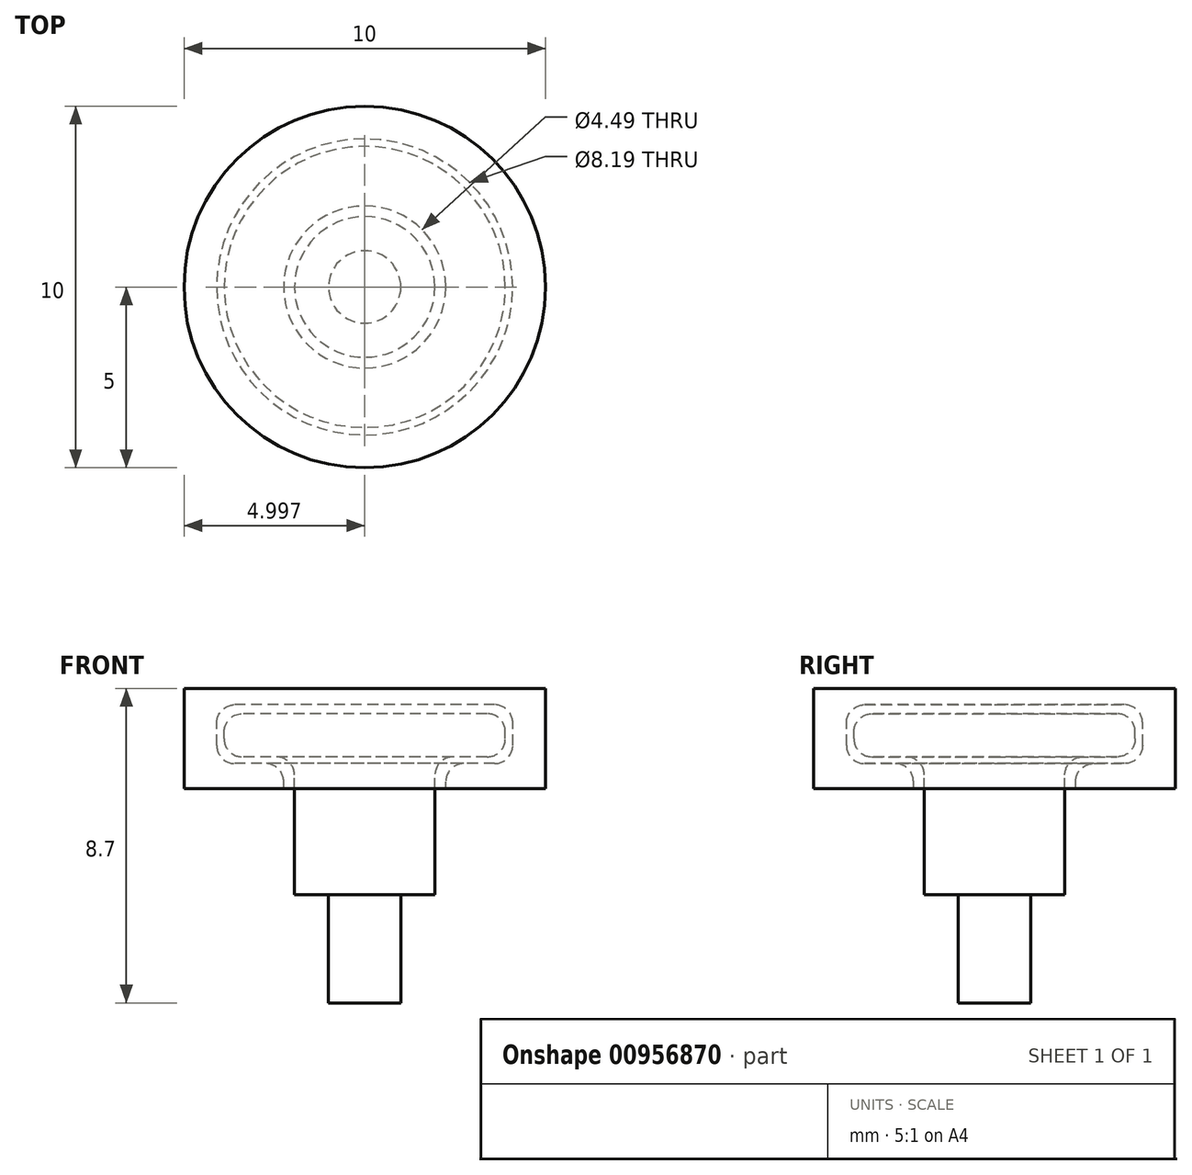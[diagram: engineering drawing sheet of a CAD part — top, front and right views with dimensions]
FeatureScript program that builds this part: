
annotation { "Feature Type Name" : "Feature", "Feature Type Description" : "" }
export const myFeature = defineFeature(function(context is Context, id is Id, definition is map)
    precondition{}
    {
        {
            var Q0;
            Q0=qCreatedBy(makeId("Front.planeOp"),FACE);
            var sketch = newSketch(context, id + "F0", { "sketchPlane" : qUnion([Q0])});
            skLineSegment(sketch, "E0.bottom", {"start": v(-2.43, 2.08) * mm, "end": v(0.96, 2.08) * mm});
            skLineSegment(sketch, "E0.top", {"start": v(-2.43, 0.88) * mm, "end": v(-1.49, 0.88) * mm});
            skLineSegment(sketch, "E0.left", {"start": v(-2.93, 1.58) * mm, "end": v(-2.93, 1.38) * mm});
            skLineSegment(sketch, "E0.right", {"start": v(0.96, 2.08) * mm, "end": v(0.96, 0.88) * mm});
            skLineSegment(sketch, "E1.bottom", {"start": v(-0.99, 2.08) * mm, "end": v(0.96, 2.08) * mm});
            skLineSegment(sketch, "E1.top", {"start": v(-0.99, -2.92) * mm, "end": v(0.96, -2.92) * mm});
            skLineSegment(sketch, "E1.left", {"start": v(-0.99, 0.38) * mm, "end": v(-0.99, -2.92) * mm});
            skLineSegment(sketch, "E1.right", {"start": v(0.96, 2.08) * mm, "end": v(0.96, -2.92) * mm});
            skLineSegment(sketch, "E2.bottom", {"start": v(-1.79, 0.7) * mm, "end": v(-2.64, 0.7) * mm});
            skLineSegment(sketch, "E2.top", {"start": v(-1.29, 0) * mm, "end": v(-4.04, 0) * mm});
            skLineSegment(sketch, "E2.left", {"start": v(-1.29, 0.2) * mm, "end": v(-1.29, 0) * mm});
            skLineSegment(sketch, "E2.right", {"start": v(-4.04, 0.7) * mm, "end": v(-4.04, 0) * mm});
            skLineSegment(sketch, "E3.bottom", {"start": v(-4.04, 0) * mm, "end": v(-3.14, 0) * mm});
            skLineSegment(sketch, "E3.top", {"start": v(-4.04, 2.78) * mm, "end": v(-3.14, 2.78) * mm});
            skLineSegment(sketch, "E3.left", {"start": v(-4.04, 0) * mm, "end": v(-4.04, 2.78) * mm});
            skLineSegment(sketch, "E3.right", {"start": v(-3.14, 1.2) * mm, "end": v(-3.14, 1.83) * mm});
            skLineSegment(sketch, "E4.bottom", {"start": v(-4.04, 2.78) * mm, "end": v(0.96, 2.78) * mm});
            skLineSegment(sketch, "E4.top", {"start": v(-2.64, 2.33) * mm, "end": v(0.96, 2.33) * mm});
            skLineSegment(sketch, "E4.left", {"start": v(-4.04, 2.78) * mm, "end": v(-4.04, 2.33) * mm});
            skLineSegment(sketch, "E4.right", {"start": v(0.96, 2.78) * mm, "end": v(0.96, 2.33) * mm});
            skPoint(sketch, "E5.visualSharp", {"position": v(-2.93, 2.08) * mm});
            skArc(sketch, "E5.filletArc", {"start": v(-2.43, 2.08) * mm, "mid": v(-2.79, 1.93) * mm, "end": v(-2.93, 1.58) * mm});
            skPoint(sketch, "E6.visualSharp", {"position": v(-2.93, 0.88) * mm});
            skArc(sketch, "E6.filletArc", {"start": v(-2.93, 1.38) * mm, "mid": v(-2.79, 1.03) * mm, "end": v(-2.43, 0.88) * mm});
            skPoint(sketch, "E7.visualSharp", {"position": v(-0.99, 0.88) * mm});
            skArc(sketch, "E7.filletArc", {"start": v(-0.99, 0.38) * mm, "mid": v(-1.13, 0.74) * mm, "end": v(-1.49, 0.88) * mm});
            skPoint(sketch, "E8.visualSharp", {"position": v(-3.14, 0.7) * mm});
            skArc(sketch, "E8.filletArc", {"start": v(-3.14, 1.2) * mm, "mid": v(-3, 0.85) * mm, "end": v(-2.64, 0.7) * mm});
            skPoint(sketch, "E9.visualSharp", {"position": v(-3.14, 2.33) * mm});
            skArc(sketch, "E9.filletArc", {"start": v(-2.64, 2.33) * mm, "mid": v(-3, 2.18) * mm, "end": v(-3.14, 1.83) * mm});
            skPoint(sketch, "E10.visualSharp", {"position": v(-1.29, 0.7) * mm});
            skArc(sketch, "E10.filletArc", {"start": v(-1.29, 0.2) * mm, "mid": v(-1.43, 0.55) * mm, "end": v(-1.79, 0.7) * mm});
            skSolve(sketch);
        }
        {
            var Q0;
            Q0=makeQuery(id+"F0.imprint","IMPRINT",FACE,{"disambiguationData":[TD([[makeQuery(id+"F0.imprint","IMPRINT",EDGE,{"derivedFrom":sQuery(id+"F0.wireOp",EDGE,"E2.bottom")}),1.0]])]});
            var Q1;
            Q1=makeQuery(id+"F0.imprint","IMPRINT",FACE,{"disambiguationData":[TD([[makeQuery(id+"F0.imprint","IMPRINT",EDGE,{"derivedFrom":sQuery(id+"F0.wireOp",EDGE,"E0.bottom")}),-1.0]])]});
            var Q2;
            Q2=sQuery(id+"F0.wireOp",EDGE,"E1.right");
            revolve(context, id + "F1", {"surfaceOperationType" : NewSurfaceOperationType.NEW, "entities" : qUnion([Q0, Q1]), "axis" : qUnion([Q2]), "revolveType" : RevolveType.FULL});
        }
        {
            var Q0;
            Q0=makeQuery(id+"F1.opRevolve","SWEPT_FACE",FACE,{"disambiguationData":[OSD([sQuery(id+"F0.wireOp",EDGE,"E1.top")])]});
            var sketch = newSketch(context, id + "F2", { "sketchPlane" : qUnion([Q0])});
            skCircle(sketch, "E11", {"center": v(0.96, 0) * mm, "radius": 1 * mm});
            skSolve(sketch);
        }
        {
            var Q0;
            Q0=makeQuery(id+"F2.imprint","IMPRINT",FACE,{"disambiguationData":[TD([[makeQuery(id+"F2.imprint","IMPRINT",EDGE,{"derivedFrom":sQuery(id+"F2.wireOp",EDGE,"E11")}),1.0]])]});
            extrude(context, id + "F3", {"entities" : qUnion([Q0]), "operationType" : NewBodyOperationType.ADD, "depth" : 3 * mm, "offsetDistance" : 25 * mm});
        }
    });
